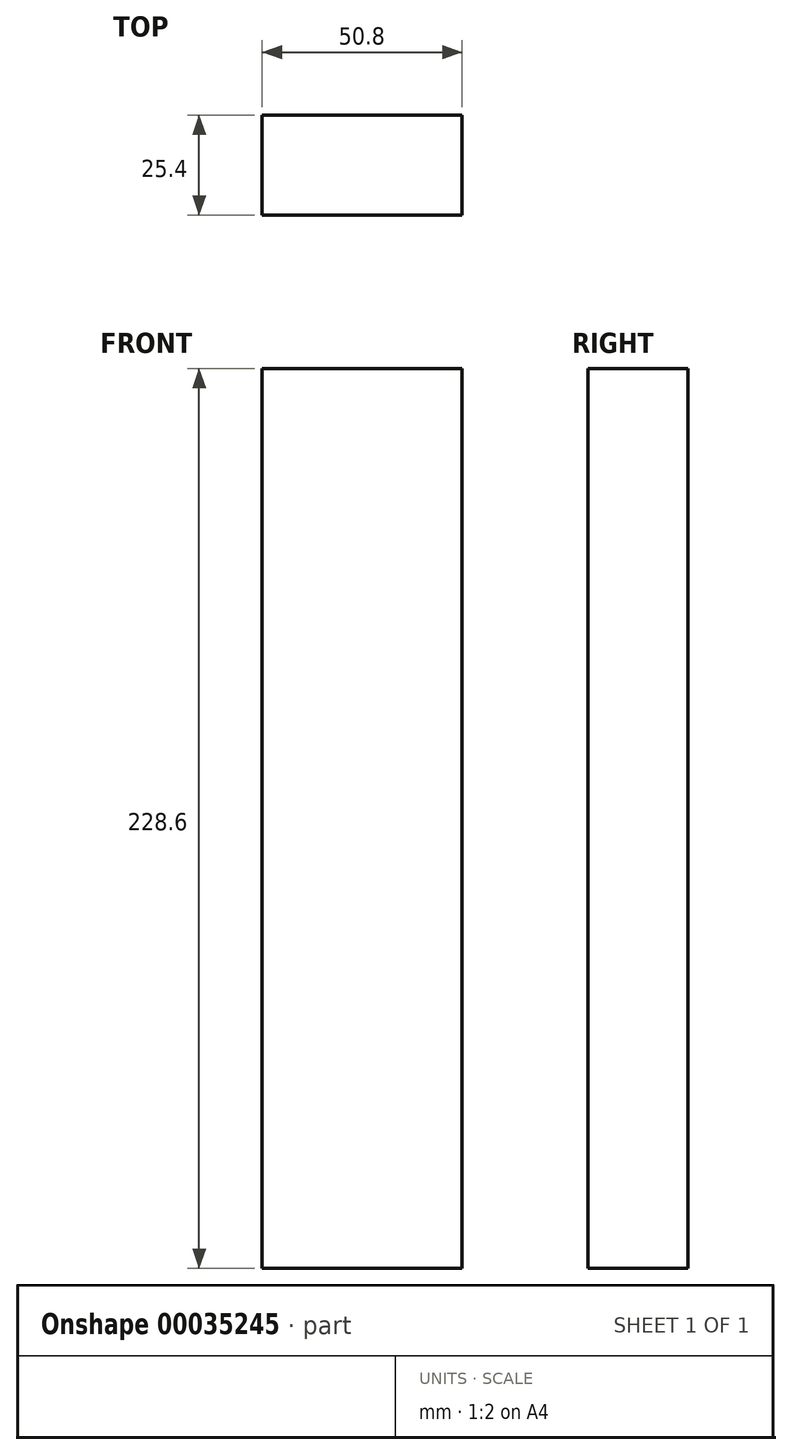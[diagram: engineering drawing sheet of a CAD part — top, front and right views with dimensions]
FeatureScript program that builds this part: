
annotation { "Feature Type Name" : "Feature", "Feature Type Description" : "" }
export const myFeature = defineFeature(function(context is Context, id is Id, definition is map)
    precondition{}
    {
        {
            var Q0;
            Q0=qCreatedBy(makeId("Front.planeOp"),FACE);
            var sketch = newSketch(context, id + "F0", { "sketchPlane" : qUnion([Q0])});
            skLineSegment(sketch, "E0.rect.bottom", {"start": v(25.4, -114.3) * mm, "end": v(-25.4, -114.3) * mm});
            skLineSegment(sketch, "E0.rect.top", {"start": v(25.4, 114.3) * mm, "end": v(-25.4, 114.3) * mm});
            skLineSegment(sketch, "E0.rect.left", {"start": v(25.4, -114.3) * mm, "end": v(25.4, 114.3) * mm});
            skLineSegment(sketch, "E0.rect.right", {"start": v(-25.4, -114.3) * mm, "end": v(-25.4, 114.3) * mm});
            skPoint(sketch, "E0.rect.middle", {"position": v(0, 0) * mm});
            skSolve(sketch);
        }
        {
            var Q0;
            Q0 = qSketchRegion(id + "F0", true);
            extrude(context, id + "F1", {"entities" : qUnion([Q0]), "depth" : 25.4 * mm});
        }
    });
